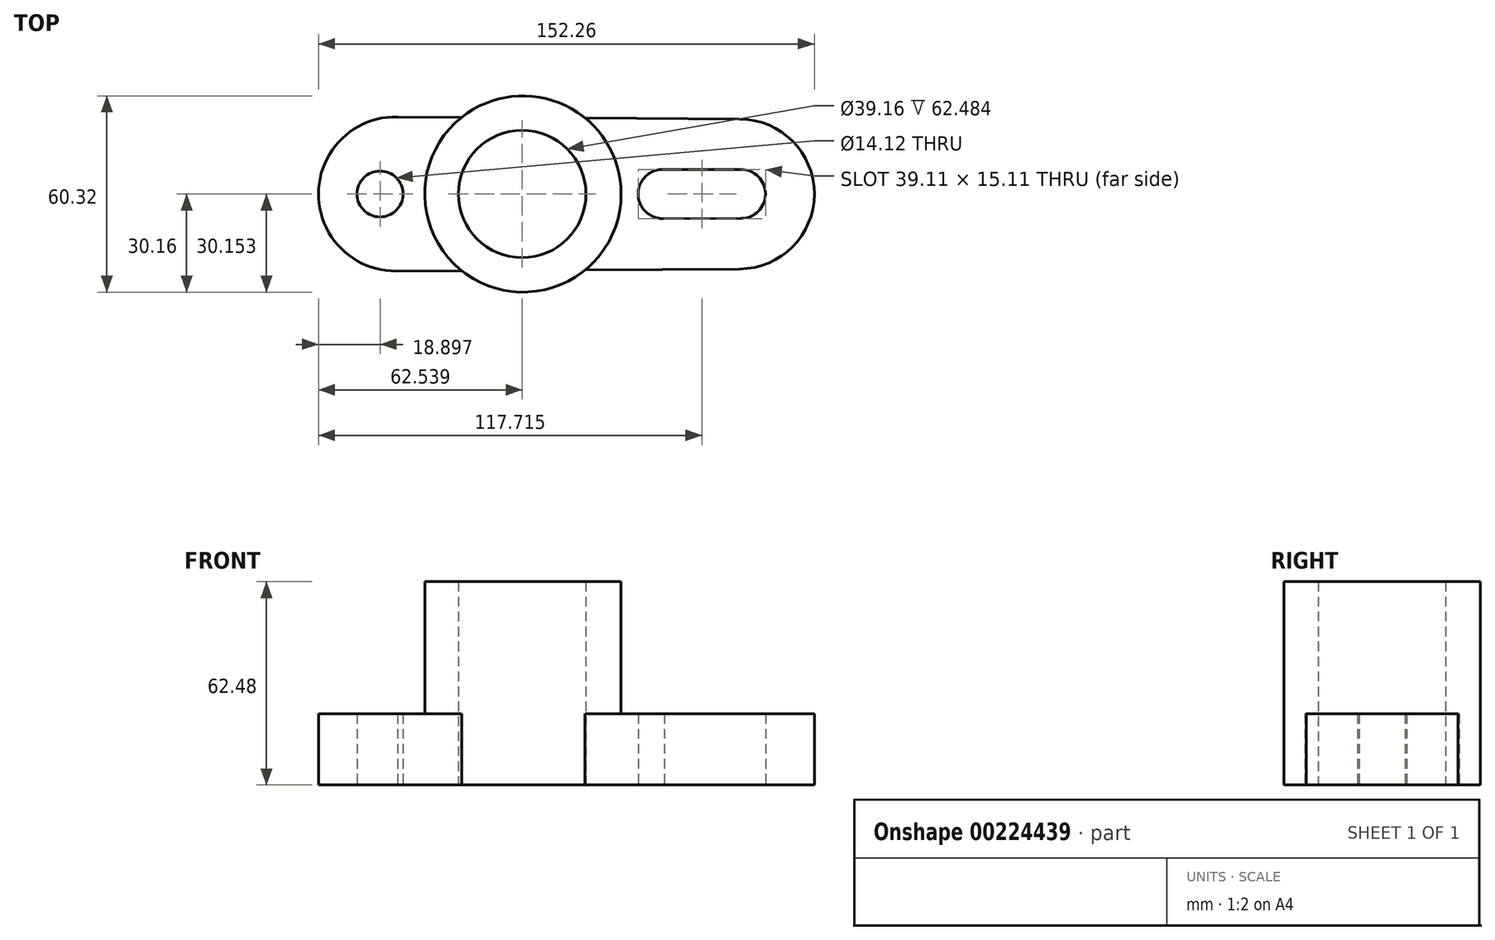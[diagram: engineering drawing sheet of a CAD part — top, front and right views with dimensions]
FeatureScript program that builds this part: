
annotation { "Feature Type Name" : "Feature", "Feature Type Description" : "" }
export const myFeature = defineFeature(function(context is Context, id is Id, definition is map)
    precondition{}
    {
        {
            var Q0;
            Q0=qCreatedBy(makeId("Top.planeOp"),FACE);
            var sketch = newSketch(context, id + "F0", { "sketchPlane" : qUnion([Q0])});
            skArc(sketch, "E0", {"start": v(-61.58, 23.7) * mm, "mid": v(-85.82, 0.2) * mm, "end": v(-61.96, -23.7) * mm});
            skArc(sketch, "E1", {"start": v(43.56, -23.03) * mm, "mid": v(66.44, 0) * mm, "end": v(43.56, 23.03) * mm});
            skLineSegment(sketch, "E2", {"start": v(-62.35, 23.7) * mm, "end": v(43.56, 23.03) * mm});
            skLineSegment(sketch, "E3", {"start": v(43.56, -23.03) * mm, "end": v(-61.96, -23.7) * mm});
            skPoint(sketch, "E4.center.orphan", {"position": v(-6.2, 0) * mm});
            skCircle(sketch, "E5", {"center": v(-22.81, 0) * mm, "radius": 29.96 * mm});
            skSolve(sketch);
        }
        {
            var Q0;
            Q0 = qSketchRegion(id + "F0", true);
            extrude(context, id + "F1", {"entities" : qUnion([Q0]), "depth" : 21.84 * mm});
        }
        {
            var Q0;
            Q0=qCreatedBy(makeId("Top.planeOp"),FACE);
            var sketch = newSketch(context, id + "F2", { "sketchPlane" : qUnion([Q0])});
            skCircle(sketch, "E6", {"center": v(-23.05, 0) * mm, "radius": 30.16 * mm});
            skSolve(sketch);
        }
        {
            var Q0;
            Q0 = qSketchRegion(id + "F2", true);
            extrude(context, id + "F3", {"entities" : qUnion([Q0]), "operationType" : NewBodyOperationType.ADD, "depth" : 62.48 * mm});
        }
        {
            var Q0;
            Q0=qCreatedBy(makeId("Top.planeOp"),FACE);
            var sketch = newSketch(context, id + "F4", { "sketchPlane" : qUnion([Q0])});
            skCircle(sketch, "E7", {"center": v(-23.28, 0) * mm, "radius": 19.58 * mm});
            skSolve(sketch);
        }
        {
            var Q0;
            Q0 = qSketchRegion(id + "F4", true);
            extrude(context, id + "F5", {"entities" : qUnion([Q0]), "operationType" : NewBodyOperationType.REMOVE, "depth" : 62.74 * mm});
        }
        {
            var Q0;
            Q0=qCreatedBy(makeId("Top.planeOp"),FACE);
            var sketch = newSketch(context, id + "F6", { "sketchPlane" : qUnion([Q0])});
            skCircle(sketch, "E8", {"center": v(43.91, 0) * mm, "radius": 7.54 * mm});
            skCircle(sketch, "E9", {"center": v(19.9, 0) * mm, "radius": 7.56 * mm});
            skLineSegment(sketch, "E10", {"start": v(20.35, 7.55) * mm, "end": v(43.92, 7.54) * mm});
            skLineSegment(sketch, "E11", {"start": v(43.92, 7.54) * mm, "end": v(43.91, -7.54) * mm});
            skLineSegment(sketch, "E12", {"start": v(43.91, -7.54) * mm, "end": v(19.9, -7.56) * mm});
            skSolve(sketch);
        }
        {
            var Q0;
            Q0 = qSketchRegion(id + "F6", true);
            extrude(context, id + "F7", {"entities" : qUnion([Q0]), "operationType" : NewBodyOperationType.REMOVE, "depth" : 23.88 * mm});
        }
        {
            var Q0;
            Q0=qCreatedBy(makeId("Top.planeOp"),FACE);
            var sketch = newSketch(context, id + "F8", { "sketchPlane" : qUnion([Q0])});
            skCircle(sketch, "E13", {"center": v(-66.92, 0) * mm, "radius": 7.06 * mm});
            skSolve(sketch);
        }
        {
            var Q0;
            Q0 = qSketchRegion(id + "F8", true);
            extrude(context, id + "F9", {"entities" : qUnion([Q0]), "operationType" : NewBodyOperationType.REMOVE, "depth" : 33.02 * mm});
        }
    });
